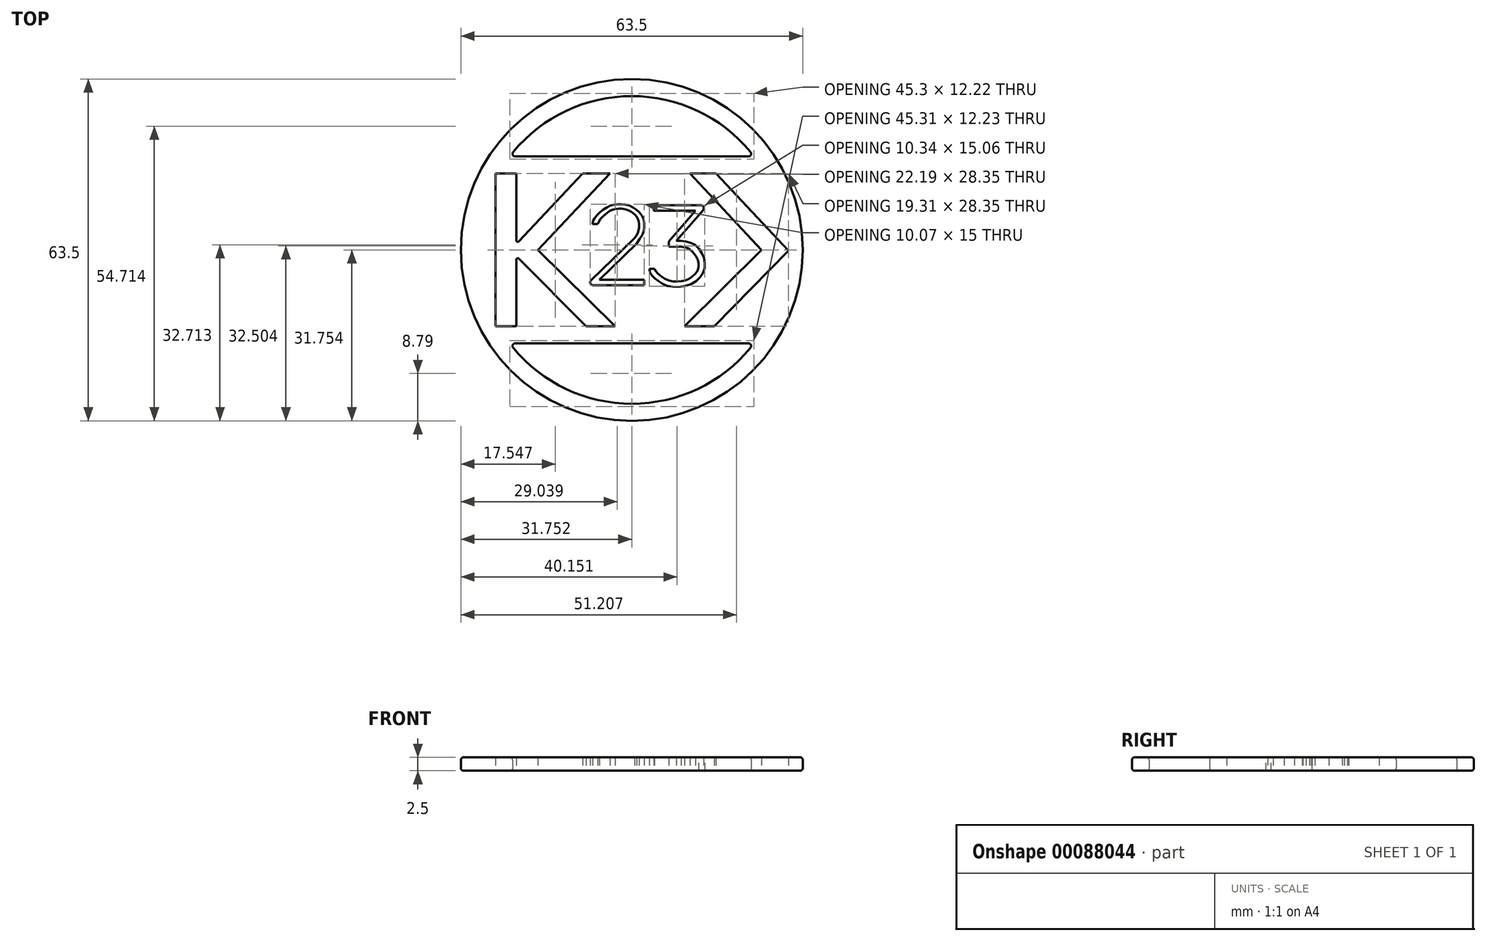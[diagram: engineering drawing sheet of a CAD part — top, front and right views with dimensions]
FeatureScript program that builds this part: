
annotation { "Feature Type Name" : "Feature", "Feature Type Description" : "" }
export const myFeature = defineFeature(function(context is Context, id is Id, definition is map)
    precondition{}
    {
        {
            var Q0;
            Q0=qCreatedBy(makeId("Top.planeOp"),FACE);
            var sketch = newSketch(context, id + "F0", { "sketchPlane" : qUnion([Q0])});
            skLineSegment(sketch, "E0", {"start": v(-0.89, -6.86) * mm, "end": v(-0.89, -5.86) * mm});
            skLineSegment(sketch, "E1", {"start": v(-0.89, -6.86) * mm, "end": v(-10.45, -6.86) * mm});
            skLineSegment(sketch, "E2", {"start": v(-10.8, -5.98) * mm, "end": v(-2.71, 1.9) * mm});
            skLineSegment(sketch, "E3", {"start": v(-0.89, -5.86) * mm, "end": v(-9.24, -5.86) * mm});
            skLineSegment(sketch, "E4", {"start": v(-9.24, -5.86) * mm, "end": v(-9.94, -5.14) * mm, "construction": true});
            skLineSegment(sketch, "E5", {"start": v(-9.24, -5.86) * mm, "end": v(-2.33, 0.87) * mm});
            skFitSpline(sketch, "E6", {"points": [v(-2.71, 1.9) * mm, v(-2.16, 2.67) * mm, v(-1.91, 3.51) * mm, v(-1.87, 4.73) * mm, v(-2.2, 5.68) * mm, v(-2.98, 6.54) * mm, v(-4.08, 7.15) * mm, v(-5.4, 7.35) * mm, v(-6.5, 7.25) * mm, v(-7.4, 6.85) * mm, v(-8.4, 6.08) * mm, v(-9.1, 5.32) * mm, v(-9.52, 4.5) * mm], "startDerivative": vector(10.41, 10.64) * mm, "endDerivative": vector(-4.73, -10.96) * mm});
            skLineSegment(sketch, "E7", {"start": v(-9.52, 4.5) * mm, "end": v(-10.52, 4.5) * mm});
            skFitSpline(sketch, "E8", {"points": [v(-10.52, 4.5) * mm, v(-10.38, 5.12) * mm, v(-9.89, 5.86) * mm, v(-9, 6.8) * mm, v(-8.15, 7.4) * mm, v(-7.07, 7.95) * mm, v(-6.06, 8.15) * mm, v(-5.1, 8.18) * mm, v(-3.88, 7.98) * mm, v(-2.73, 7.42) * mm, v(-1.96, 6.83) * mm, v(-1.2, 5.87) * mm, v(-0.92, 4.7) * mm, v(-0.95, 3.49) * mm, v(-1.21, 2.6) * mm, v(-2.33, 0.87) * mm], "startDerivative": vector(1.92, 12.36) * mm, "endDerivative": vector(-15.52, -18.51) * mm});
            skLineSegment(sketch, "E9", {"start": v(0.87, 7.96) * mm, "end": v(0.87, 6.96) * mm});
            skLineSegment(sketch, "E10", {"start": v(0.87, 7.96) * mm, "end": v(9.66, 7.96) * mm});
            skLineSegment(sketch, "E11", {"start": v(10.04, 7.12) * mm, "end": v(5.08, 1.4) * mm});
            skLineSegment(sketch, "E12", {"start": v(0.87, 6.96) * mm, "end": v(8.58, 6.96) * mm});
            skLineSegment(sketch, "E13", {"start": v(8.58, 6.96) * mm, "end": v(9.34, 6.3) * mm});
            skLineSegment(sketch, "E14", {"start": v(8.58, 6.96) * mm, "end": v(3.66, 1.27) * mm});
            skLineSegment(sketch, "E15", {"start": v(3.66, 1.27) * mm, "end": v(3.66, 0.27) * mm});
            skPoint(sketch, "E16.visualSharp", {"position": v(10.77, 7.96) * mm});
            skArc(sketch, "E16.filletArc", {"start": v(10.04, 7.12) * mm, "mid": v(10.12, 7.67) * mm, "end": v(9.66, 7.96) * mm});
            skPoint(sketch, "E17.visualSharp", {"position": v(-11.7, -6.86) * mm});
            skArc(sketch, "E17.filletArc", {"start": v(-10.8, -5.98) * mm, "mid": v(-10.92, -6.54) * mm, "end": v(-10.45, -6.86) * mm});
            skLineSegment(sketch, "E18", {"start": v(3.66, 0.27) * mm, "end": v(5.98, 0.27) * mm});
            skFitSpline(sketch, "E19", {"points": [v(5.98, 0.27) * mm, v(6.76, 0.12) * mm, v(7.63, -0.25) * mm, v(8.28, -0.87) * mm, v(8.8, -1.63) * mm, v(9.2, -2.74) * mm, v(9.08, -4.01) * mm, v(8.14, -5.15) * mm, v(6.97, -5.92) * mm, v(5.75, -6.17) * mm, v(3.96, -6.08) * mm, v(2.44, -5.35) * mm, v(1.38, -4.46) * mm, v(1.02, -3.8) * mm], "startDerivative": vector(12.2, -1.75) * mm, "endDerivative": vector(-3.87, 14.26) * mm});
            skLineSegment(sketch, "E20", {"start": v(1.02, -3.8) * mm, "end": v(0.02, -3.8) * mm});
            skFitSpline(sketch, "E21", {"points": [v(0.02, -3.8) * mm, v(0.23, -4.61) * mm, v(0.64, -5.22) * mm, v(1.43, -5.89) * mm, v(2.63, -6.69) * mm, v(4.01, -7.1) * mm, v(6.25, -7.1) * mm, v(8.27, -6.47) * mm, v(9.62, -5.2) * mm, v(10.28, -3.96) * mm, v(10.32, -2.38) * mm, v(9.9, -1.11) * mm, v(8.87, 0.35) * mm, v(7.63, 1.05) * mm, v(6.08, 1.36) * mm, v(5.08, 1.4) * mm], "startDerivative": vector(0.7, -15.69) * mm, "endDerivative": vector(-16.7, -0.1) * mm});
            skLineSegment(sketch, "E22", {"start": v(12.4, 13.86) * mm, "end": v(25.9, -0.46) * mm});
            skLineSegment(sketch, "E23", {"start": v(25.9, -0.46) * mm, "end": v(12.1, -14.5) * mm});
            skLineSegment(sketch, "E24", {"start": v(12.1, -14.5) * mm, "end": v(6.6, -14.5) * mm});
            skLineSegment(sketch, "E25", {"start": v(-28.5, -14.5) * mm, "end": v(-28.5, 13.86) * mm});
            skLineSegment(sketch, "E26", {"start": v(-24.66, 13.86) * mm, "end": v(-24.66, 1.43) * mm});
            skLineSegment(sketch, "E27", {"start": v(-11.73, -14.5) * mm, "end": v(-24.23, -1.95) * mm});
            skLineSegment(sketch, "E28", {"start": v(-6.32, -14.5) * mm, "end": v(-20.66, -0.35) * mm});
            skLineSegment(sketch, "E29", {"start": v(-20.66, -0.35) * mm, "end": v(-7.28, 13.86) * mm});
            skLineSegment(sketch, "E30", {"start": v(-24.22, 1.26) * mm, "end": v(-12.36, 13.86) * mm});
            skLineSegment(sketch, "E31", {"start": v(6.6, -14.5) * mm, "end": v(20.87, -0.32) * mm});
            skLineSegment(sketch, "E32", {"start": v(20.87, -0.32) * mm, "end": v(7.57, 13.86) * mm});
            skLineSegment(sketch, "E33.trimOffspring", {"start": v(7.57, 13.86) * mm, "end": v(12.4, 13.86) * mm});
            skLineSegment(sketch, "E34.trimOffspring", {"start": v(-12.36, 13.86) * mm, "end": v(-7.28, 13.86) * mm});
            skLineSegment(sketch, "E35.trimOffspring", {"start": v(-24.66, -2.13) * mm, "end": v(-24.66, -14.5) * mm});
            skLineSegment(sketch, "E36.trimOffspring", {"start": v(-24.66, -14.5) * mm, "end": v(-28.5, -14.5) * mm});
            skLineSegment(sketch, "E37.trimOffspring", {"start": v(-6.32, -14.5) * mm, "end": v(-11.73, -14.5) * mm});
            skLineSegment(sketch, "E38", {"start": v(25.9, -14.5) * mm, "end": v(25.9, 13.86) * mm, "construction": true});
            skLineSegment(sketch, "E39", {"start": v(25.9, 13.86) * mm, "end": v(-28.5, 13.86) * mm, "construction": true});
            skLineSegment(sketch, "E40", {"start": v(-24.66, 13.86) * mm, "end": v(-28.5, 13.86) * mm});
            skLineSegment(sketch, "E41", {"start": v(-28.5, 13.86) * mm, "end": v(-28.5, -14.5) * mm, "construction": true});
            skLineSegment(sketch, "E42", {"start": v(25.9, -14.5) * mm, "end": v(-28.5, -14.5) * mm, "construction": true});
            skCircle(sketch, "E43", {"center": v(-3.2, -0.32) * mm, "radius": 31.75 * mm});
            skLineSegment(sketch, "E44", {"start": v(25.9, -0.32) * mm, "end": v(39.63, -0.32) * mm, "construction": true});
            skLineSegment(sketch, "E45", {"start": v(-1.3, 18.1) * mm, "end": v(-1.3, 13.86) * mm, "construction": true});
            skLineSegment(sketch, "E46", {"start": v(25.9, -0.32) * mm, "end": v(-28.5, -0.32) * mm, "construction": true});
            skLineSegment(sketch, "E47", {"start": v(-1.3, 13.86) * mm, "end": v(-1.3, -0.32) * mm, "construction": true});
            skArc(sketch, "E48.0", {"start": v(-25.26, -18.5) * mm, "mid": v(-3.2, -28.9) * mm, "end": v(18.84, -18.5) * mm});
            skLineSegment(sketch, "E49", {"start": v(-24.86, 17.03) * mm, "end": v(18.44, 17.03) * mm});
            skLineSegment(sketch, "E50", {"start": v(-24.86, -17.67) * mm, "end": v(18.45, -17.67) * mm});
            skArc(sketch, "E51.trimOffspring", {"start": v(18.83, 17.86) * mm, "mid": v(-3.2, 28.26) * mm, "end": v(-25.25, 17.86) * mm});
            skPoint(sketch, "E52.visualSharp", {"position": v(-25.91, 17.03) * mm});
            skArc(sketch, "E52.filletArc", {"start": v(-25.25, 17.86) * mm, "mid": v(-25.32, 17.32) * mm, "end": v(-24.86, 17.03) * mm});
            skPoint(sketch, "E53.visualSharp", {"position": v(19.5, 17.03) * mm});
            skArc(sketch, "E53.filletArc", {"start": v(18.44, 17.03) * mm, "mid": v(18.9, 17.32) * mm, "end": v(18.83, 17.86) * mm});
            skPoint(sketch, "E54.visualSharp", {"position": v(-25.92, -17.67) * mm});
            skArc(sketch, "E54.filletArc", {"start": v(-24.86, -17.67) * mm, "mid": v(-25.32, -17.96) * mm, "end": v(-25.26, -18.5) * mm});
            skPoint(sketch, "E55.visualSharp", {"position": v(19.5, -17.67) * mm});
            skArc(sketch, "E55.filletArc", {"start": v(18.84, -18.5) * mm, "mid": v(18.9, -17.96) * mm, "end": v(18.45, -17.67) * mm});
            skPoint(sketch, "E56.visualSharp", {"position": v(-24.66, 0.8) * mm});
            skArc(sketch, "E56.filletArc", {"start": v(-24.66, 1.43) * mm, "mid": v(-24.5, 1.2) * mm, "end": v(-24.22, 1.26) * mm});
            skPoint(sketch, "E57.visualSharp", {"position": v(-24.66, -1.52) * mm});
            skArc(sketch, "E57.filletArc", {"start": v(-24.23, -1.95) * mm, "mid": v(-24.5, -1.9) * mm, "end": v(-24.66, -2.13) * mm});
            skSolve(sketch);
        }
        {
            var Q0;
            Q0=makeQuery(id+"F0.imprint","IMPRINT",FACE,{"disambiguationData":[TD([[makeQuery(id+"F0.imprint","IMPRINT",EDGE,{"derivedFrom":sQuery(id+"F0.wireOp",EDGE,"E0")}),-1.0]])]});
            extrude(context, id + "F1", {"entities" : qUnion([Q0]), "depth" : 2.5 * mm});
        }
        {
            var Q0;
            Q0=makeQuery(id+"F1.opExtrude","CAP_EDGE",EDGE,{"disambiguationData":[OSD([sQuery(id+"F0.wireOp",EDGE,"E43")])],"isStart":false});
            var Q1;
            Q1=makeQuery(id+"F1.opExtrude","CAP_EDGE",EDGE,{"disambiguationData":[OSD([sQuery(id+"F0.wireOp",EDGE,"E50")])],"isStart":false});
            var Q2;
            Q2=makeQuery(id+"F1.opExtrude","CAP_EDGE",EDGE,{"disambiguationData":[OSD([sQuery(id+"F0.wireOp",EDGE,"E49")])],"isStart":false});
            var Q3;
            Q3=makeQuery(id+"F1.opExtrude","CAP_EDGE",EDGE,{"disambiguationData":[OSD([sQuery(id+"F0.wireOp",EDGE,"E43")])],"isStart":true});
            var Q4;
            Q4=makeQuery(id+"F1.opExtrude","CAP_EDGE",EDGE,{"disambiguationData":[OSD([sQuery(id+"F0.wireOp",EDGE,"E48.0")])],"isStart":true});
            var Q5;
            Q5=makeQuery(id+"F1.opExtrude","CAP_EDGE",EDGE,{"disambiguationData":[OSD([sQuery(id+"F0.wireOp",EDGE,"E51.trimOffspring")])],"isStart":true});
            fillet(context, id + "F2", {"entities" : qUnion([Q0, Q1, Q2, Q3, Q4, Q5]), "radius" : .5 * mm, "tangentPropagation" : true, "allowEdgeOverflow" : false});
        }
    });
